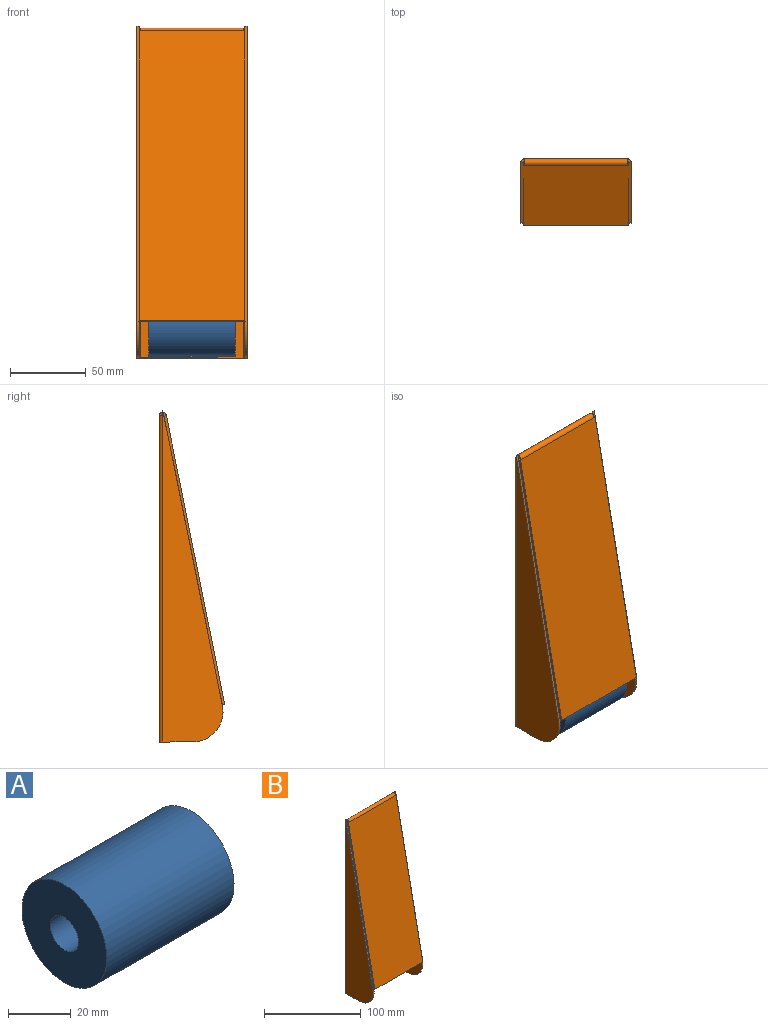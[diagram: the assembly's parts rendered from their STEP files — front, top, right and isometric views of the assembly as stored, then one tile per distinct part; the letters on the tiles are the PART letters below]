
ASSEMBLY  parts=2 mates=1
PART A: 4 faces, bbox 57.2x38.1x38.1 mm
  f0: cylinder r=6.35mm len=57.15mm, axis (-1,0,0), area 2280.2mm2, adj f2,f3
  f1: cylinder r=19.05mm len=57.15mm, axis (-1,0,0), area 6840.6mm2, adj f2,f3
  f2: plane 38.1x38.1mm, normal (1,0,0), area 1013.4mm2, adj f0,f1
  f3: plane 38.1x38.1mm, normal (-1,0,0), area 1013.4mm2, adj f0,f1
PART B: 36 faces, bbox 73x43.4x219.6 mm
  f0: plane 3.72x1.59mm, normal (0,1,0), area 5.9mm2, adj f3,f5,f6,f29
  f1: plane 1.59x0.03mm, normal (0,0.2,0.98), area 0mm2, adj f2,f3,f5,f6
  f2: cylinder r=20.32mm len=24.34mm, axis (1,0,0), area 57.1mm2, adj f1,f4,f5,f6
  f3: plane 195.28x39.45mm, normal (0,-0.98,0.2), area 316.3mm2, adj f0,f1,f5,f6
  f4: plane 19.56x1.59mm, normal (0,0,-1), area 31mm2, adj f2,f5,f6,f28
  f5: plane 219.62x39.88mm, normal (-1,0,0), area 4733.4mm2, adj f0,f1,f2,f3,f4,f30
  f6: plane 219.62x39.88mm, normal (1,0,0), area 4733.4mm2, adj f0,f1,f2,f3,f4,f31
  f7: plane 1.59x0.03mm, normal (0,0.2,0.98), area 0mm2, adj f8,f11,f12,f13
  f8: cylinder r=20.32mm len=24.34mm, axis (1,0,0), area 57.1mm2, adj f7,f9,f12,f13
  f9: plane 19.56x1.59mm, normal (0,0,-1), area 31mm2, adj f8,f12,f13,f32
  f10: plane 3.72x1.59mm, normal (0,1,0), area 5.9mm2, adj f11,f12,f13,f33
  f11: plane 195.28x39.45mm, normal (0,-0.98,0.2), area 316.3mm2, adj f7,f10,f12,f13
  f12: plane 219.62x39.88mm, normal (1,0,0), area 4733.4mm2, adj f7,f8,f9,f10,f11,f34
  f13: plane 219.62x39.88mm, normal (-1,0,0), area 4733.4mm2, adj f7,f8,f9,f10,f11,f35
  f14: plane 1.56x0.74mm, normal (0,0.2,0.98), area 1.2mm2, adj f15,f19,f20,f25
  f15: plane 192.02x40.28mm, normal (1,0,0), area 310.5mm2, adj f14,f18,f19,f20
  f16: plane 1.56x0.74mm, normal (0,0.2,0.98), area 1.2mm2, adj f17,f19,f20,f24
  f17: plane 192.02x40.28mm, normal (-1,0,0), area 310.5mm2, adj f16,f18,f19,f20
  f18: plane 69.8x1.56mm, normal (0,-0.2,-0.98), area 110.8mm2, adj f15,f17,f19,f20
  f19: plane 191.71x69.8mm, normal (0,-0.98,0.2), area 13651.3mm2, adj f14,f15,f16,f17,f18,f26
  f20: plane 191.71x69.8mm, normal (0,0.98,-0.2), area 13651.3mm2, adj f14,f15,f16,f17,f18,f27
  f21: plane 68.33x1.59mm, normal (0,0,-1), area 108.5mm2, adj f22,f23,f28,f32
  f22: plane 215.9x68.33mm, normal (0,1,0), area 14751.6mm2, adj f21,f26,f30,f34
  f23: plane 215.9x68.33mm, normal (0,-1,0), area 14751.6mm2, adj f21,f27,f31,f35
  f24: plane 4.65x2.35mm, normal (-1,0,0), area 7.3mm2, adj f16,f26,f27,f29
  f25: plane 4.65x2.35mm, normal (1,0,0), area 7.3mm2, adj f14,f26,f27,f33
  f26: cylinder r=2.35mm len=68.33mm, axis (-1,0,0), area 472.3mm2, adj f19,f22,f24,f25
  f27: cylinder r=0.76mm len=68.33mm, axis (-1,0,0), area 153.2mm2, adj f20,f23,f24,f25
  f28: plane 2.35x2.35mm, normal (0,0,-1), area 3.9mm2, adj f4,f21,f30,f31
  f29: plane 2.35x2.35mm, normal (0,0,1), area 3.9mm2, adj f0,f24,f30,f31
  f30: cylinder r=2.35mm len=215.9mm, axis (0,0,-1), area 796.8mm2, adj f5,f22,f28,f29
  f31: cylinder r=0.76mm len=215.9mm, axis (0,0,-1), area 258.4mm2, adj f6,f23,f28,f29
  f32: plane 2.35x2.35mm, normal (0,0,-1), area 3.9mm2, adj f9,f21,f34,f35
  f33: plane 2.35x2.35mm, normal (0,0,1), area 3.9mm2, adj f10,f25,f34,f35
  f34: cylinder r=2.35mm len=215.9mm, axis (0,0,-1), area 796.8mm2, adj f12,f22,f32,f33
  f35: cylinder r=0.76mm len=215.9mm, axis (0,0,-1), area 258.4mm2, adj f13,f23,f32,f33
PLACE A rot(axis=(1,0,0),0deg) t=(34.92,-20.32,20.32)mm
PLACE B at identity fixed
MATE fastened B.f2 <-> A.f1  axis (-1,0,0) through (34.93,-20.32,20.32)mm
